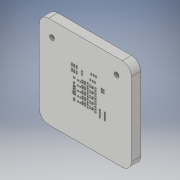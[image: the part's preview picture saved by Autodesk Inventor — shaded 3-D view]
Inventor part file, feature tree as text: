
AUTODESK INVENTOR PART (.ipt)
format: ipt  version: 2019.3 (Build 233278000, 278)  size: 581,120 bytes
history: native  units: mm
features: extrude x1, fillet x1
ambient origin geometry x8: Origin, YZ Plane, XZ Plane, XY Plane, X Axis, Y Axis, Z Axis, Center Point
bodies: Body1 (feature_tree)
feature tree (2):
  extrude  "Extrusion4"  Depth=100.0mm
  fillet  "Fillet2"  Radius=100.0mm
